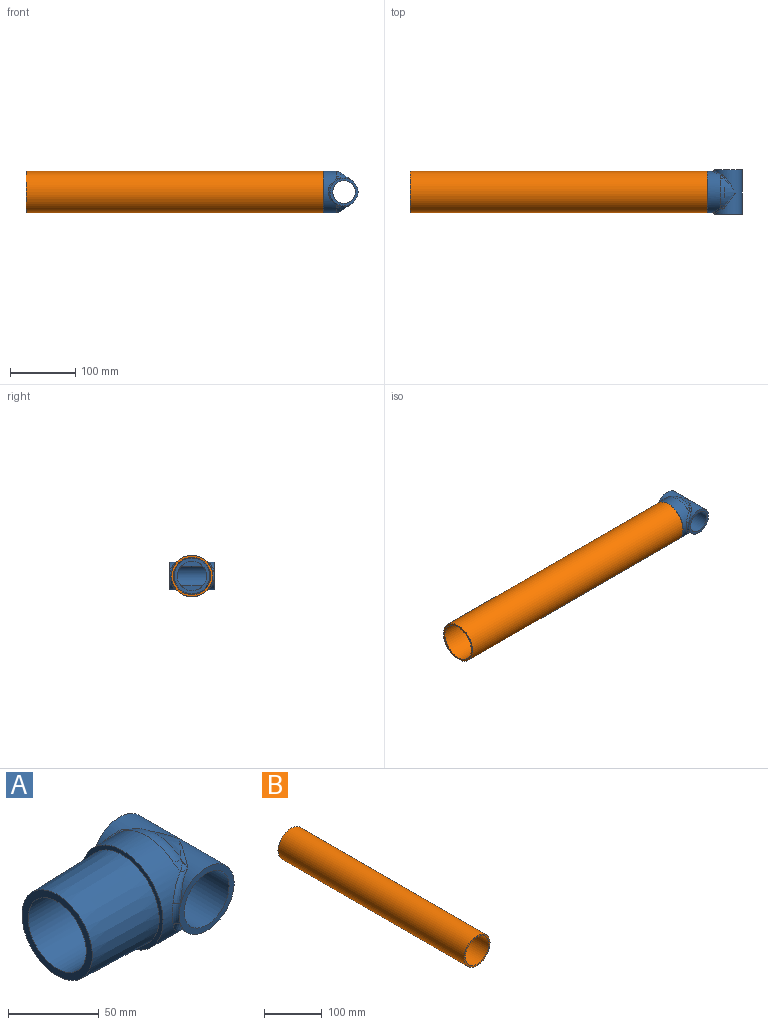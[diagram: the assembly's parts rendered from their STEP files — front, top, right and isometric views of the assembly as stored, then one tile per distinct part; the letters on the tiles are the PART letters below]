
ASSEMBLY  parts=2 mates=1
PART A: 33 faces, bbox 104x68.9x68.8 mm
  f0: cylinder r=17.46mm len=68mm, axis (0,1,0), area 6073.5mm2, adj f8,f9,f30,f31,f32
  f1: cone r=31.75mm half-angle=34.5deg, axis (-1,0,0), area 383.7mm2, adj f14,f19,f27
  f2: cone r=31.75mm half-angle=34.5deg, axis (-1,0,0), area 383.7mm2, adj f10,f15,f22
  f3: cylinder r=31.75mm len=63.5mm, axis (1,0,0), area 3277.1mm2, adj f4,f11,f12,f13,f16,f17,f18,f21
  f4: plane 63.5x63.5mm, normal (-1,0,0), area 569.7mm2, adj f3,f5
  f5: cone r=28.75mm half-angle=1.5deg, axis (1,0,0), area 8968.3mm2, adj f4,f6
  f6: plane 54.85x54.85mm, normal (-1,0,0), area 749.3mm2, adj f5,f30
  f7: cylinder r=21.37mm len=68mm, axis (0,1,0), area 4775.5mm2, adj f8,f9,f10,f11,f13,f14,f15,f16
  f8: plane 42.81x42.81mm, normal (0,-1,0), area 476.4mm2, adj f0,f7,f17
  f9: plane 42.81x42.81mm, normal (0,1,0), area 476.4mm2, adj f0,f7,f12
  f10: bspline ~29.06x23.96mm, area 39.9mm2, adj f2,f7,f20,f21
  f11: bspline ~19.21x17.1mm, area 76.9mm2, adj f3,f7,f12,f20
  f12: bspline ~16.36x4.58mm, area 60.6mm2, adj f3,f9,f11,f13
  f13: bspline ~17.93x16.13mm, area 76.9mm2, adj f3,f7,f12,f29
  f14: bspline ~28.04x23.12mm, area 39.9mm2, adj f1,f7,f28,f29
  f15: bspline ~28.04x23.12mm, area 39.9mm2, adj f2,f7,f23,f24
  f16: bspline ~17.93x16.13mm, area 76.9mm2, adj f3,f7,f17,f24
  f17: bspline ~16.36x4.58mm, area 60.6mm2, adj f3,f8,f16,f18
  f18: bspline ~19.21x17.1mm, area 76.9mm2, adj f3,f7,f17,f25
  f19: bspline ~29.06x23.96mm, area 39.9mm2, adj f1,f7,f25,f26
  f20: bspline ~5.69x5.21mm, area 8.8mm2, adj f10,f11,f21
  f21: bspline ~7.66x6.89mm, area 26.2mm2, adj f3,f10,f20,f22
  f22: torus R=19.05mm, axis (-1,0,0), area 337.9mm2, adj f2,f3,f21,f23
  f23: bspline ~7.66x6.9mm, area 26.2mm2, adj f3,f15,f22,f24
  f24: bspline ~5.97x5.51mm, area 8.8mm2, adj f15,f16,f23
  f25: bspline ~5.69x5.21mm, area 8.8mm2, adj f18,f19,f26
  f26: bspline ~7.66x6.89mm, area 26.2mm2, adj f3,f19,f25,f27
  f27: torus R=19.05mm, axis (-1,0,0), area 337.9mm2, adj f1,f3,f26,f28
  f28: bspline ~7.66x6.9mm, area 26.2mm2, adj f3,f14,f27,f29
  f29: bspline ~5.97x5.51mm, area 8.8mm2, adj f13,f14,f28
  f30: cylinder r=22.66mm len=73.03mm, axis (-1,0,0), area 10144.5mm2, adj f0,f6,f31,f32
  f31: plane 34.6x8.02mm, normal (-1,0,0), area 192.8mm2, adj f0,f30
  f32: plane 34.6x8.02mm, normal (-1,0,0), area 192.8mm2, adj f0,f30
PART B: 4 faces, bbox 63.5x457.2x63.5 mm
  f0: cylinder r=28.75mm len=457.2mm, axis (0,-1,0), area 82597.4mm2, adj f2,f3
  f1: cylinder r=31.75mm len=457.2mm, axis (0,-1,0), area 91207.3mm2, adj f2,f3
  f2: plane 63.5x63.5mm, normal (0,1,0), area 569.7mm2, adj f0,f1
  f3: plane 63.5x63.5mm, normal (0,-1,0), area 569.7mm2, adj f0,f1
PLACE A t=(30.58,0.02,0.03)mm fixed
PLACE B rot(axis=(-0.58,0.58,0.58),120deg) t=(-1.17,0.02,0.03)mm
MATE fastened B.f1 <-> A.f1  axis (1,0,0) through (-1.17,0.02,0.03)mm
